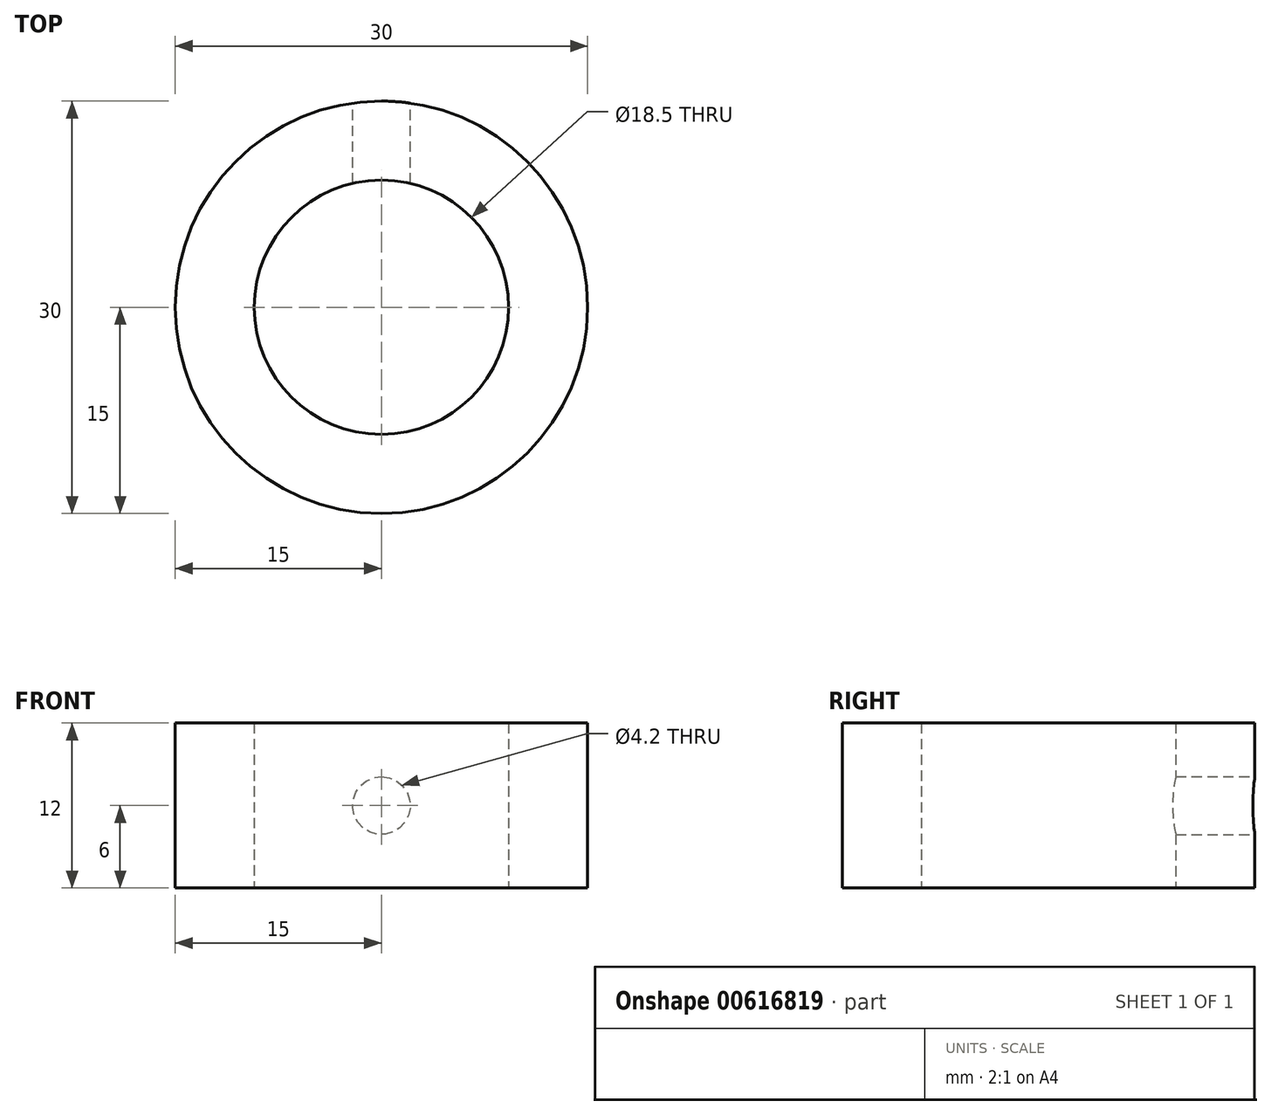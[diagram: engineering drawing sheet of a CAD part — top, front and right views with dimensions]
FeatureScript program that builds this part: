
annotation { "Feature Type Name" : "Feature", "Feature Type Description" : "" }
export const myFeature = defineFeature(function(context is Context, id is Id, definition is map)
    precondition{}
    {
        {
            var Q0;
            Q0=qCreatedBy(makeId("Top.planeOp"),FACE);
            var sketch = newSketch(context, id + "F0", { "sketchPlane" : qUnion([Q0])});
            skCircle(sketch, "E0", {"center": v(0, 0) * mm, "radius": 9.25 * mm});
            skCircle(sketch, "E1", {"center": v(0, 0) * mm, "radius": 15 * mm});
            skSolve(sketch);
        }
        {
            var Q0;
            Q0 = qSketchRegion(id + "F0", true);
            extrude(context, id + "F1", {"entities" : qUnion([Q0]), "depth" : 12 * mm, "offsetDistance" : 25 * mm});
        }
        {
            var Q0;
            Q0=qCreatedBy(makeId("Front.planeOp"),FACE);
            var sketch = newSketch(context, id + "F2", { "sketchPlane" : qUnion([Q0])});
            skPoint(sketch, "E2", {"position": v(0, 6) * mm});
            skSolve(sketch);
        }
        {
            var Q0;
            Q0=sQuery(id+"F2.wireOp",VERTEX,"E2");
            var Q1;
            Q1=makeQuery(id+"F1.opExtrude","SWEPT_BODY",BODY,{"disambiguationData":[OSD([sQuery(id+"F0.wireOp",EDGE,"E0"),sQuery(id+"F0.wireOp",EDGE,"E1")])]});
            hole(context, id + "F3", {"style" : HoleStyle.SIMPLE, "endStyle" : HoleEndStyle.THROUGH, "standardTappedOrClearance" : lookupTablePath({ "standard" : "ISO", "engagement" : "75%", "pitch" : "0.8 mm", "size" : "M5", "type" : "Tapped" }), "standardBlindInLast" : lookupTablePath({ "standard" : "ISO", "engagement" : "75%", "pitch" : "0.8 mm", "size" : "M5", "type" : "Tapped" }), "holeDiameter" : 4.2 * mm, "majorDiameter" : 5 * mm, "showTappedDepth" : true, "isTappedThrough" : true, "tappedDepth" : 3.9 * mm, "tapClearance" : 3, "locations" : qUnion([Q0]), "scope" : qUnion([Q1]), "startStyle" : HoleStartStyle.PART});
        }
    });
